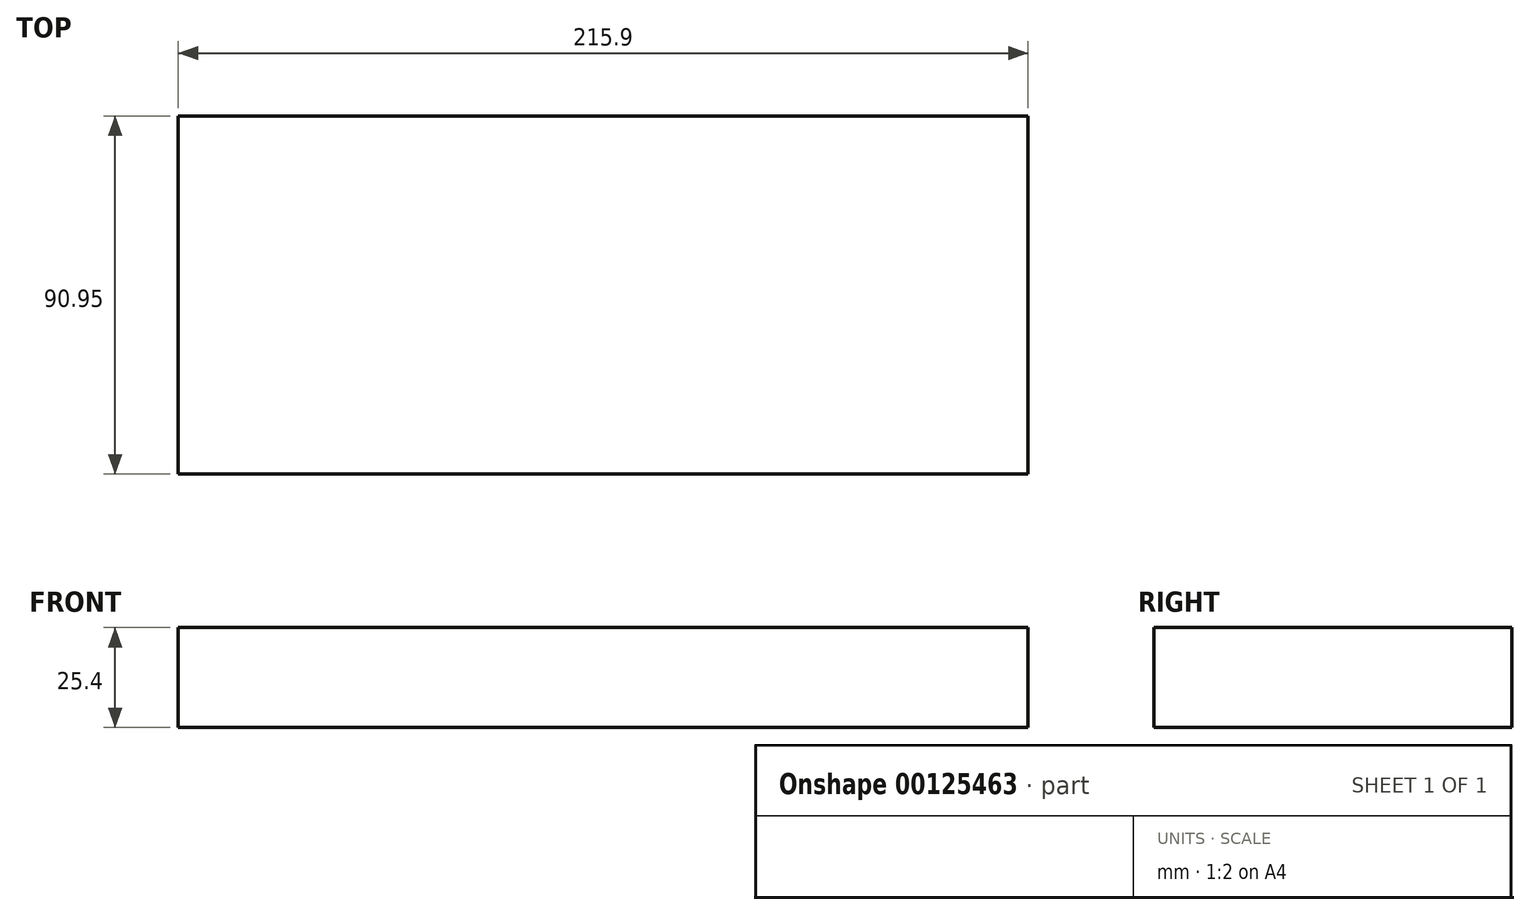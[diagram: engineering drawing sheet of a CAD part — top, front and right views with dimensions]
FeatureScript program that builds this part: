
annotation { "Feature Type Name" : "Feature", "Feature Type Description" : "" }
export const myFeature = defineFeature(function(context is Context, id is Id, definition is map)
    precondition{}
    {
        {
            var Q0;
            Q0=qCreatedBy(makeId("Top.planeOp"),FACE);
            var sketch = newSketch(context, id + "F0", { "sketchPlane" : qUnion([Q0])});
            skLineSegment(sketch, "E0.bottom", {"start": v(0, 0) * mm, "end": v(215.9, 0) * mm});
            skLineSegment(sketch, "E0.top", {"start": v(0, -90.95) * mm, "end": v(215.9, -90.95) * mm});
            skLineSegment(sketch, "E0.left", {"start": v(0, 0) * mm, "end": v(0, -90.95) * mm});
            skLineSegment(sketch, "E0.right", {"start": v(215.9, 0) * mm, "end": v(215.9, -90.95) * mm});
            skSolve(sketch);
        }
        {
            var Q0;
            Q0=makeQuery(id+"F0.imprint","IMPRINT",FACE,{"disambiguationData":[TD([[makeQuery(id+"F0.imprint","IMPRINT",EDGE,{"derivedFrom":sQuery(id+"F0.wireOp",EDGE,"E0.bottom")}),-1.0]])]});
            extrude(context, id + "F1", {"entities" : qUnion([Q0]), "depth" : 25.4 * mm});
        }
    });
